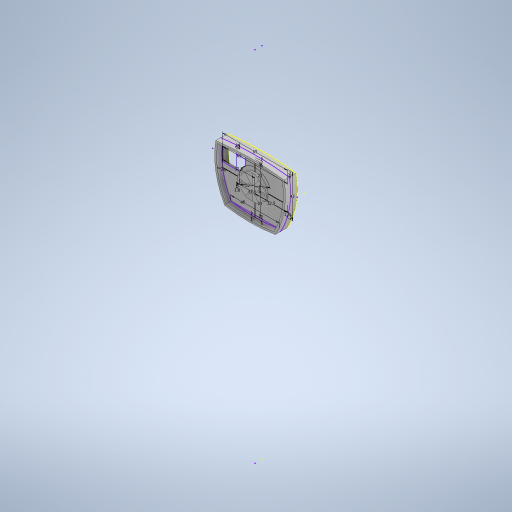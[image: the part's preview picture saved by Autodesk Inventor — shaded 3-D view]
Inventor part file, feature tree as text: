
AUTODESK INVENTOR PART (.ipt)
format: ipt  version: 2023 (Build 270158000, 158)  size: 482,816 bytes
history: mixed  units: in
note: dims shown in document units (in); Inventor stores cm internally (conversion verified against a paired STEP export)
features: extrude x14, sketch x8, projected_geometry x1, imported_body x1
ambient origin geometry x8: Origin, YZ Plane, XZ Plane, XY Plane, X Axis, Y Axis, Z Axis, Center Point
bodies: Solid1 (imported_parasolid), Body1 (imported_parasolid)
feature tree (24):
  extrude  "Extrusion5"  Depth=0.3937in
  sketch  "Sketch5"  dims[d13=0.9843in d18=2.5591in]
  extrude  "Extrusion6"  Depth=2.5591in
  extrude  "Extrusion7"  Depth=0.0787in
  extrude  "Extrusion8"  Depth=1.2795in
  extrude  "Extrusion9"  Depth=0.0787in
  sketch  "Sketch7"  dims[d21=1.2795in d22=1.2795in]
  extrude  "Extrusion10"  Depth=1.8898in
  extrude  "Extrusion12"  Depth=0.2756in TaperAngle=0.0deg
  extrude  "Extrusion14"  Depth=0.2362in
  extrude  "Extrusion15"  Depth=0.3937in TaperAngle=0.0deg
  extrude  "Extrusion16"  Depth=2.0315in
  extrude  "Extrusion17"  Depth=1.6535in
  extrude  "Extrusion18"  Depth=0.0787in
  extrude  "Extrusion19"  Depth=0.0787in
  extrude  "Extrusion20"  Depth=0.0787in
  sketch  "Sketch1"  dims[d10=0.3937in d11=0.0in d12=0.9055in]
  sketch  "Sketch6"  dims[d19=0.0787in d20=0.0787in]
  sketch  "Sketch8"  dims[d23=0.0787in d24=0.0787in]
  sketch  "Sketch10"  dims[d25=2.5591in d26=1.8898in]
  sketch  "Sketch11"  dims[d27=0.0787in d28=0.0in d29=0.2756in d30=0.0in]
  projected_geometry  "Projected Loop1"
  sketch  "Sketch12"  dims[d31=0.6693in d32=0.0in d33=1.2598in d36=0.3937in d37=0.0in d39=2.0315in d40=1.6535in d41=0.0787in d42=0.0787in d44=0.0787in d50=0.2756in d51=0.0in d54=0.0787in d55=0.0in d66=0.1969in d67=0.0709in d68=0.1969in d69=0.0709in d70=0.2362in d71=0.0in d72=0.2362in d73=0.0in d74=0.1181in d75=0.1181in d76=0.1969in d77=0.1181in d78=0.1969in d79=0.1181in d80=0.1969in d81=0.0in d82=0.1969in d83=0.0in d84=0.1181in d85=0.0in d86=0.0in d87=0.0in d88=0.0787in d89=0.0787in d90=0.2362in d91=0.0in d0=0.0197in d1=1.9685in d2=0.0197in d3=1.9685in]
  imported_body  NMx_Import_Brep_tag  [imported B-rep: ~47 faces, bbox_mm=[68.464898, 51.606881, 12.0]]
